# Revit family: Pivot-Door_Series-7200_2-Panel_All-Weather
name_source: partatom
category: Doors
units: mm (PartAtom-declared; Revit-internal decimal feet)

## family parameters
Always vertical = Yes
Classification Number = 23.30.10.14.11
Cut with Voids When Loaded = No
Host = Wall
Room Calculation Point = No
Shared = No

## types (4) — shared parameters
ADA Compliant = Yes
Analytic Construction = <None>
Define Thermal Properties by = Schematic Type
Door Glazing = Glass - Clear
Frame Finish = Metal - Stainless Steel
Frame Thickness = 0' - 6 1/8"
Function = Interior
Hardware Finish = Metal - Steel
Panel Material = Metal - Stainless Steel
Rough Width = 10' - 0"
Stop Depth = 0' - 0 5/8"
Wall Closure = By host
Width = 10' - 0"
zero-valued in all types: Expected Lifespan (Years), Maintenance Schedule (Months), R_Value, Sound Transmission Class (STC), Warranty Duration (Years)

## per-type parameters (varying)
| type | Frame Width | Height | Panel Height | Rough Height | Thickness |
| 081316_4461-107 (1 9/16) | 0' - 2 5/8" | 8' - 11" | 8' - 11" | 8' - 11" | 0' - 1 9/16" |
| 081316_4461-108 (2 5/8) | 0' - 2 3/4" | 9' - 0" | 9' - 0" | 9' - 0" | 0' - 2 5/8" |
| 081316_4461-108 (1 9/16) | 0' - 2 3/4" | 9' - 0" | 9' - 0" | 9' - 0" | 0' - 1 9/16" |
| 081316_4461-107 (2 5/8) | 0' - 2 5/8" | 8' - 11" | 8' - 11" | 8' - 11" | 0' - 2 5/8" |

## geometry (parser evidence)
native form markers: Sweep x12
no freeform markers — native parametric forms only
